# Revit family: DBXMRI
name_source: partatom
category: Lighting Fixtures
revit_build: Autodesk Revit 2014 (Build: 20130308_1515(x64)
units: mm (PartAtom-declared; Revit-internal decimal feet)

## types (1)
- DBXMRI
    Apparent Load = 0 VA
    Backbox = Aluminum - Hubbell
    Color Filter = 16777215
    Default Elevation = 48"
    Description = 6'' Dual Labeled IC/Non-IC
    Dimming Lamp Color Temperature Shift = <None>
    Emit Shape Visible in Rendering = No
    Emit from Circle Diameter = 7"
    Lamp = Incandescent
    Load Classification = Lighting
    Manufacturer = Prescolite Lighting
    Model = DBXMRI
    Photometric Notes = More IES files download in the Photometric Web Link
    Photometric Web File = dbx_tb60_75w_par30l.ies
    Photometric Web Link = https://www.hubbell.com
    Power Factor = 1
    Product Documentation Link = https://hubbellcdn.com
    Product Page URL = https://www.hubbell.com
    Tilt Angle = -90.00°
    URL = https://www.hubbell.com
    Voltage = 0 V

## geometry (parser evidence)
native form markers: Blend x5, Sweep x1
no freeform markers — native parametric forms only
